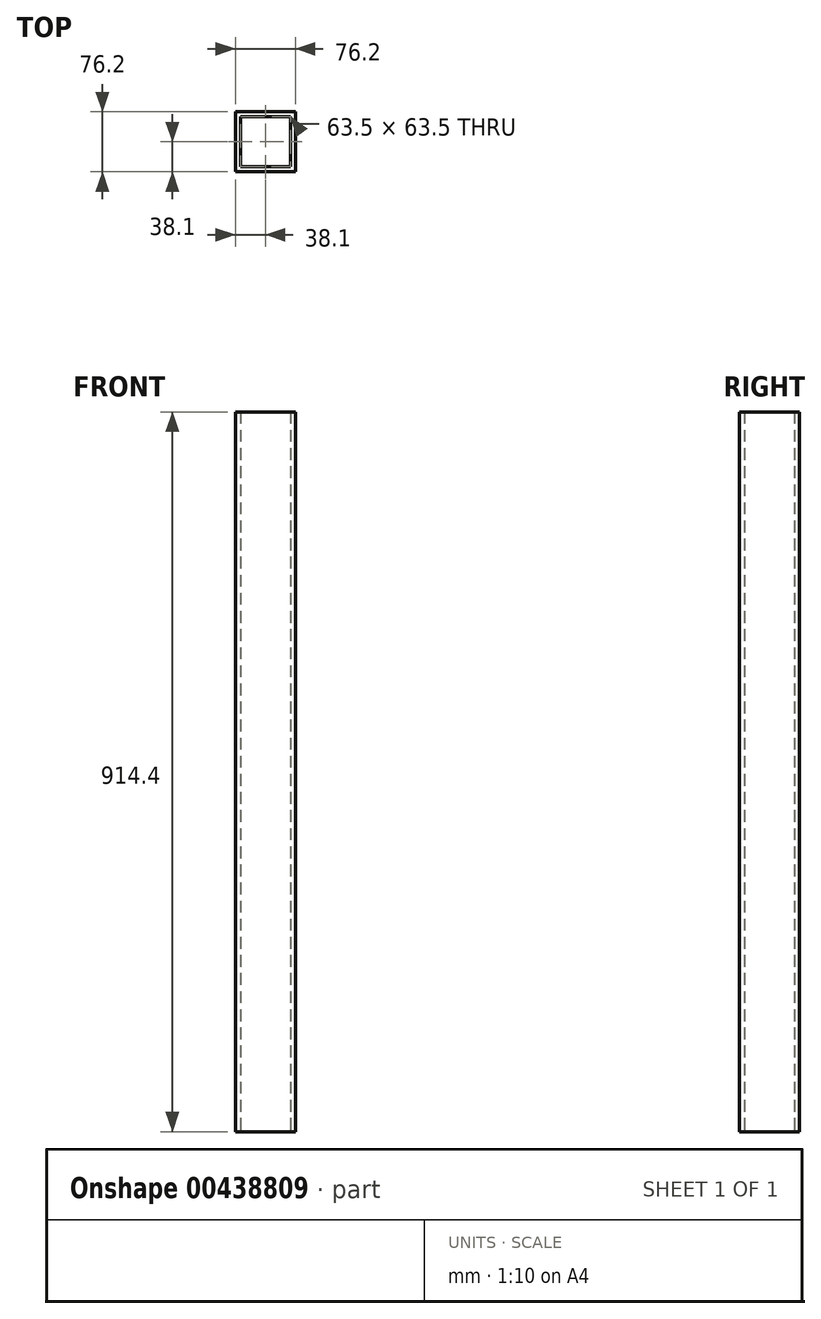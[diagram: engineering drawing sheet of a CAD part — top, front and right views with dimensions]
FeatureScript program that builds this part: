
annotation { "Feature Type Name" : "Feature", "Feature Type Description" : "" }
export const myFeature = defineFeature(function(context is Context, id is Id, definition is map)
    precondition{}
    {
        {
            var Q0;
            Q0=qCreatedBy(makeId("Top.planeOp"),FACE);
            var sketch = newSketch(context, id + "F0", { "sketchPlane" : qUnion([Q0])});
            skLineSegment(sketch, "E0.bottom", {"start": v(-76.2, -76.2) * mm, "end": v(0, -76.2) * mm});
            skLineSegment(sketch, "E0.top", {"start": v(-76.2, 0) * mm, "end": v(0, 0) * mm});
            skLineSegment(sketch, "E0.left", {"start": v(-76.2, -76.2) * mm, "end": v(-76.2, 0) * mm});
            skLineSegment(sketch, "E0.right", {"start": v(0, -76.2) * mm, "end": v(0, 0) * mm});
            skLineSegment(sketch, "E1.0", {"start": v(-6.35, -69.85) * mm, "end": v(-6.35, -6.35) * mm});
            skLineSegment(sketch, "E1.1", {"start": v(-69.85, -69.85) * mm, "end": v(-6.35, -69.85) * mm});
            skLineSegment(sketch, "E1.2", {"start": v(-69.85, -69.85) * mm, "end": v(-69.85, -6.35) * mm});
            skLineSegment(sketch, "E1.3", {"start": v(-69.85, -6.35) * mm, "end": v(-6.35, -6.35) * mm});
            skSolve(sketch);
        }
        {
            var Q0;
            Q0=makeQuery(id+"F0.imprint","IMPRINT",FACE,{"disambiguationData":[TD([[makeQuery(id+"F0.imprint","IMPRINT",EDGE,{"derivedFrom":sQuery(id+"F0.wireOp",EDGE,"E0.bottom")}),1.0]])]});
            extrude(context, id + "F1", {"entities" : qUnion([Q0]), "depth" : 914.4 * mm});
        }
    });
